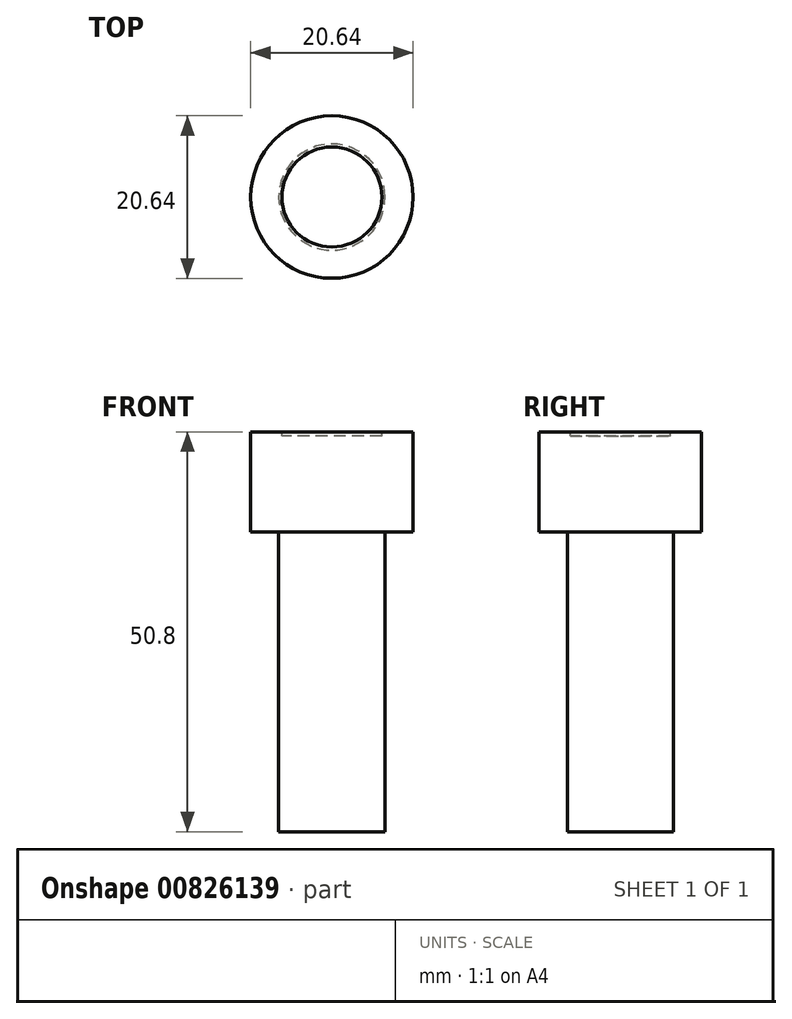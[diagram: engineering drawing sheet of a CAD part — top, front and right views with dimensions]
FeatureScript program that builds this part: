
annotation { "Feature Type Name" : "Feature", "Feature Type Description" : "" }
export const myFeature = defineFeature(function(context is Context, id is Id, definition is map)
    precondition{}
    {
        {
            var Q0;
            Q0=qCreatedBy(makeId("Top.planeOp"),FACE);
            var sketch = newSketch(context, id + "F0", { "sketchPlane" : qUnion([Q0])});
            skLineSegment(sketch, "E0", {"start": v(-32.74, 0) * mm, "end": v(32.74, 0) * mm, "construction": true});
            skCircle(sketch, "E1", {"center": v(0, 0) * mm, "radius": 6.35 * mm});
            skSolve(sketch);
        }
        {
            var Q0;
            Q0 = qSketchRegion(id + "F0", true);
            extrude(context, id + "F1", {"entities" : qUnion([Q0]), "oppositeDirection" : true, "depth" : 0.5 * mm, "offsetDistance" : 25.4 * mm});
        }
        {
            var Q0;
            Q0=qCreatedBy(makeId("Top.planeOp"),FACE);
            var sketch = newSketch(context, id + "F2", { "sketchPlane" : qUnion([Q0])});
            skCircle(sketch, "E2", {"center": v(0, 0) * mm, "radius": 5.56 * mm});
            skSolve(sketch);
        }
        {
            var Q0;
            Q0 = qSketchRegion(id + "F2", true);
            extrude(context, id + "F3", {"entities" : qUnion([Q0]), "oppositeDirection" : true, "depth" : 6.6 * mm, "offsetDistance" : 25.4 * mm});
        }
        {
            var Q0;
            Q0=makeQuery(id+"F3.opExtrude","CAP_FACE",FACE,{"disambiguationData":[OSD([sQuery(id+"F2.wireOp",EDGE,"E2")])],"isStart":false});
            var sketch = newSketch(context, id + "F4", { "sketchPlane" : qUnion([Q0])});
            skCircle(sketch, "E3", {"center": v(0, 0) * mm, "radius": 3.57 * mm});
            skSolve(sketch);
        }
        {
            var Q0;
            Q0=makeQuery(id+"F4.imprint","IMPRINT",FACE,{"disambiguationData":[TD([[makeQuery(id+"F4.imprint","IMPRINT",EDGE,{"derivedFrom":sQuery(id+"F4.wireOp",EDGE,"E3")}),1.0]])]});
            extrude(context, id + "F5", {"entities" : qUnion([Q0]), "operationType" : NewBodyOperationType.ADD, "depth" : 25.4 * mm, "offsetDistance" : 25.4 * mm});
        }
        {
            var Q0;
            Q0=qCreatedBy(makeId("Top.planeOp"),FACE);
            var sketch = newSketch(context, id + "F6", { "sketchPlane" : qUnion([Q0])});
            skCircle(sketch, "E4", {"center": v(0, 0) * mm, "radius": 6.75 * mm});
            skSolve(sketch);
        }
        {
            var Q0;
            Q0 = qSketchRegion(id + "F6", true);
            extrude(context, id + "F7", {"entities" : qUnion([Q0]), "oppositeDirection" : true, "depth" : 7.94 * mm, "offsetDistance" : 25.4 * mm});
        }
        {
            var Q0;
            Q0=makeQuery(id+"F7.opExtrude","CAP_FACE",FACE,{"disambiguationData":[OSD([sQuery(id+"F6.wireOp",EDGE,"E4")])],"isStart":false});
            var sketch = newSketch(context, id + "F8", { "sketchPlane" : qUnion([Q0])});
            skCircle(sketch, "E5", {"center": v(0, 0) * mm, "radius": 4.37 * mm});
            skSolve(sketch);
        }
        {
            var Q0;
            Q0 = qSketchRegion(id + "F8", true);
            extrude(context, id + "F9", {"entities" : qUnion([Q0]), "operationType" : NewBodyOperationType.ADD, "depth" : 25.4 * mm, "offsetDistance" : 25.4 * mm});
        }
        {
            var Q0;
            Q0=qCreatedBy(makeId("Top.planeOp"),FACE);
            var sketch = newSketch(context, id + "F10", { "sketchPlane" : qUnion([Q0])});
            skCircle(sketch, "E6", {"center": v(0, 0) * mm, "radius": 7.94 * mm});
            skSolve(sketch);
        }
        {
            var Q0;
            Q0 = qSketchRegion(id + "F10", true);
            extrude(context, id + "F11", {"entities" : qUnion([Q0]), "oppositeDirection" : true, "depth" : 9.52 * mm, "offsetDistance" : 25.4 * mm});
        }
        {
            var Q0;
            Q0=makeQuery(id+"F11.opExtrude","CAP_FACE",FACE,{"disambiguationData":[OSD([sQuery(id+"F10.wireOp",EDGE,"E6")])],"isStart":false});
            var sketch = newSketch(context, id + "F12", { "sketchPlane" : qUnion([Q0])});
            skCircle(sketch, "E7", {"center": v(0, 0) * mm, "radius": 5.16 * mm});
            skSolve(sketch);
        }
        {
            var Q0;
            Q0=makeQuery(id+"F12.imprint","IMPRINT",FACE,{"disambiguationData":[TD([[makeQuery(id+"F12.imprint","IMPRINT",EDGE,{"derivedFrom":sQuery(id+"F12.wireOp",EDGE,"E7")}),1.0]])]});
            extrude(context, id + "F13", {"entities" : qUnion([Q0]), "operationType" : NewBodyOperationType.ADD, "depth" : 25.4 * mm, "offsetDistance" : 25.4 * mm});
        }
        {
            var Q0;
            Q0=qCreatedBy(makeId("Top.planeOp"),FACE);
            var sketch = newSketch(context, id + "F14", { "sketchPlane" : qUnion([Q0])});
            skCircle(sketch, "E8", {"center": v(0, 0) * mm, "radius": 10.32 * mm});
            skSolve(sketch);
        }
        {
            var Q0;
            Q0 = qSketchRegion(id + "F14", true);
            extrude(context, id + "F15", {"entities" : qUnion([Q0]), "oppositeDirection" : true, "depth" : 12.7 * mm, "offsetDistance" : 25.4 * mm});
        }
        {
            var Q0;
            Q0=makeQuery(id+"F15.opExtrude","CAP_FACE",FACE,{"disambiguationData":[OSD([sQuery(id+"F14.wireOp",EDGE,"E8")])],"isStart":false});
            var sketch = newSketch(context, id + "F16", { "sketchPlane" : qUnion([Q0])});
            skCircle(sketch, "E9", {"center": v(0, 0) * mm, "radius": 6.75 * mm});
            skSolve(sketch);
        }
        {
            var Q0;
            Q0 = qSketchRegion(id + "F16", true);
            extrude(context, id + "F17", {"entities" : qUnion([Q0]), "operationType" : NewBodyOperationType.ADD, "depth" : 38.1 * mm, "offsetDistance" : 25.4 * mm});
        }
    });
